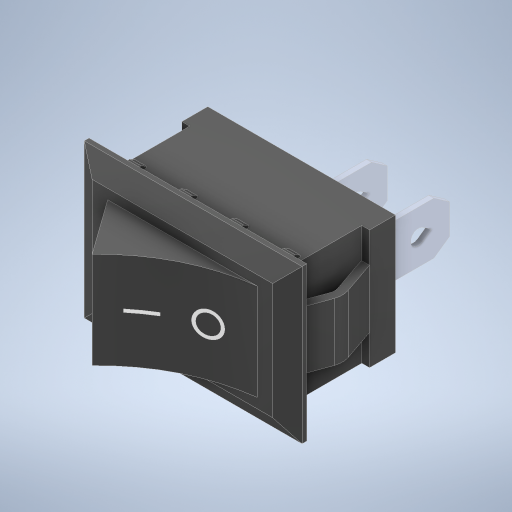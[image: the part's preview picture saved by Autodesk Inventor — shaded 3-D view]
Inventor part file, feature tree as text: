
AUTODESK INVENTOR PART (.ipt)
format: ipt  version: 2024 (Build 280153000, 153)  size: 394,752 bytes
history: native  units: mm
features: other x1, chamfer x1
ambient origin geometry x8: Origin, YZ Plane, XZ Plane, XY Plane, X Axis, Y Axis, Z Axis, Center Point
bodies: Solide1 (feature_tree)
feature tree (2):
  other  "RockerSwitch.STEP"
  chamfer  "Chamfer2"  [1 undecoded]
note: 1 required parameter value undecoded (feature->parameter linkage not recoverable at this tier; creation-order binding heuristic only, values carry confidence <= 0.55)
